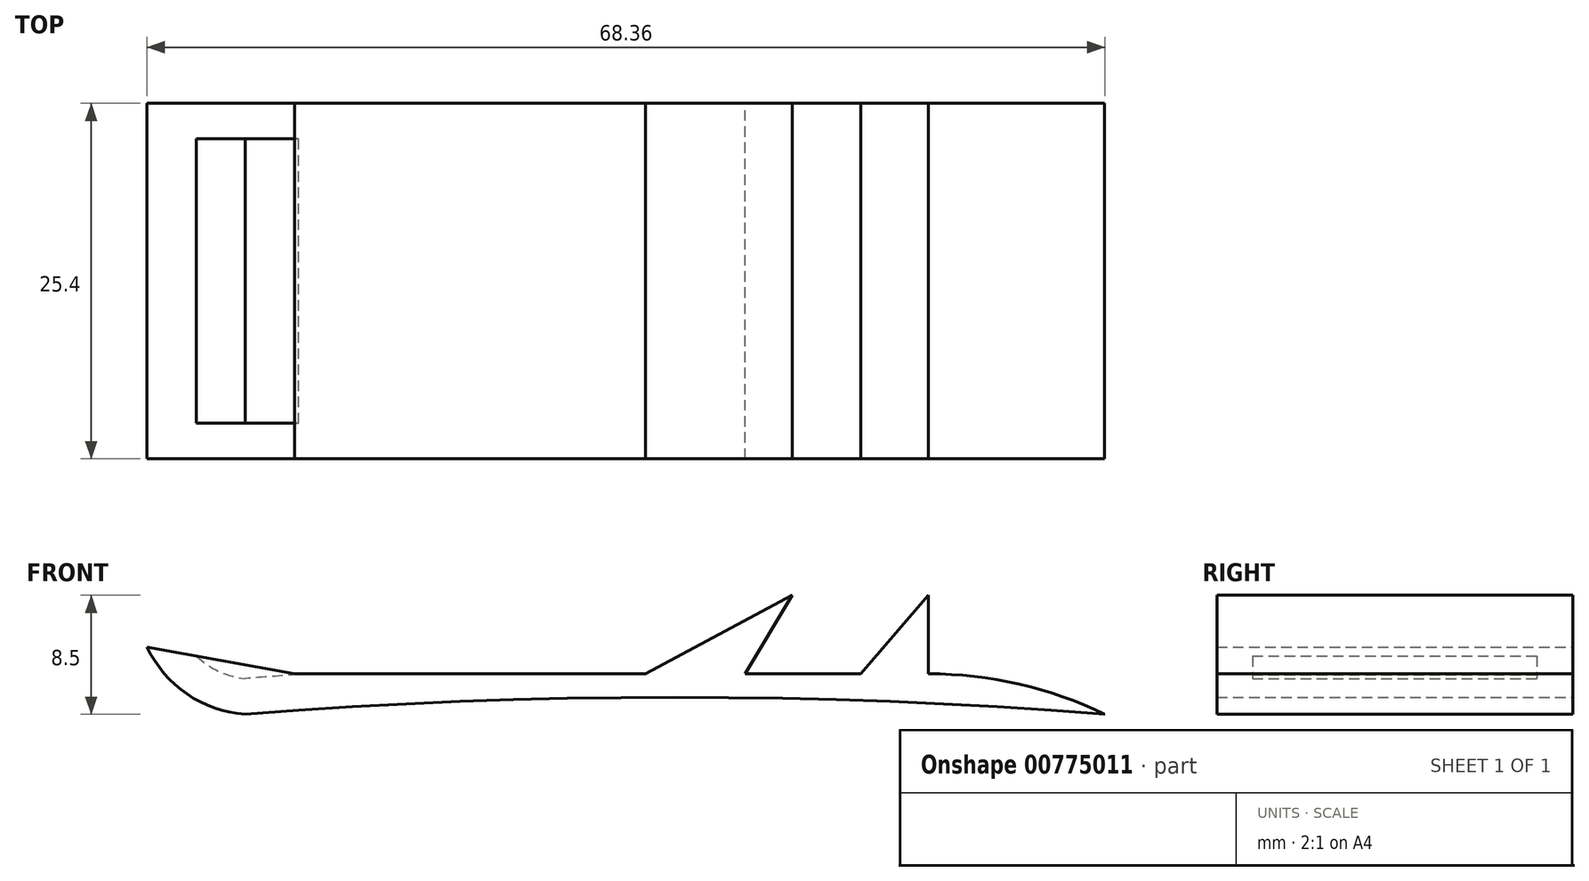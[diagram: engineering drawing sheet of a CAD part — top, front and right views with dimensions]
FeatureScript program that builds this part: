
annotation { "Feature Type Name" : "Feature", "Feature Type Description" : "" }
export const myFeature = defineFeature(function(context is Context, id is Id, definition is map)
    precondition{}
    {
        {
            var Q0;
            Q0=qCreatedBy(makeId("Front.planeOp"),FACE);
            var sketch = newSketch(context, id + "F0", { "sketchPlane" : qUnion([Q0])});
            skLineSegment(sketch, "E0", {"start": v(-32.16, 2.88) * mm, "end": v(0, 2.88) * mm});
            skLineSegment(sketch, "E1", {"start": v(8.26, 2.88) * mm, "end": v(13.1, 8.5) * mm});
            skLineSegment(sketch, "E2", {"start": v(13.1, 8.5) * mm, "end": v(13.1, 2.88) * mm});
            skLineSegment(sketch, "E3", {"start": v(13.1, 2.88) * mm, "end": v(8.26, 2.88) * mm});
            skLineSegment(sketch, "E4", {"start": v(0, 2.88) * mm, "end": v(8.26, 2.88) * mm});
            skLineSegment(sketch, "E5", {"start": v(3.38, 8.5) * mm, "end": v(0, 2.88) * mm});
            skLineSegment(sketch, "E6", {"start": v(-7.1, 2.88) * mm, "end": v(3.38, 8.5) * mm});
            skArc(sketch, "E7", {"start": v(25.68, 0) * mm, "mid": v(-5, 1.2) * mm, "end": v(-35.7, 0) * mm});
            skArc(sketch, "E8", {"start": v(25.68, 0) * mm, "mid": v(19.55, 2.15) * mm, "end": v(13.1, 2.88) * mm});
            skArc(sketch, "E9", {"start": v(-42.68, 4.8) * mm, "mid": v(-39.84, 1.45) * mm, "end": v(-35.7, 0) * mm});
            skLineSegment(sketch, "E10", {"start": v(-42.68, 4.8) * mm, "end": v(-32.16, 2.88) * mm});
            skSolve(sketch);
        }
        {
            var Q0;
            Q0 = qSketchRegion(id + "F0", true);
            extrude(context, id + "F1", {"entities" : qUnion([Q0]), "depth" : 25.4 * mm, "offsetDistance" : 25.4 * mm});
        }
        {
            var Q0;
            Q0=makeQuery(id+"F1.opExtrude","SWEPT_FACE",FACE,{"disambiguationData":[OSD([sQuery(id+"F0.wireOp",EDGE,"E10")])]});
            shell(context, id + "F2", {"entities" : qUnion([Q0]), "thickness" : 2.54 * mm});
        }
    });
